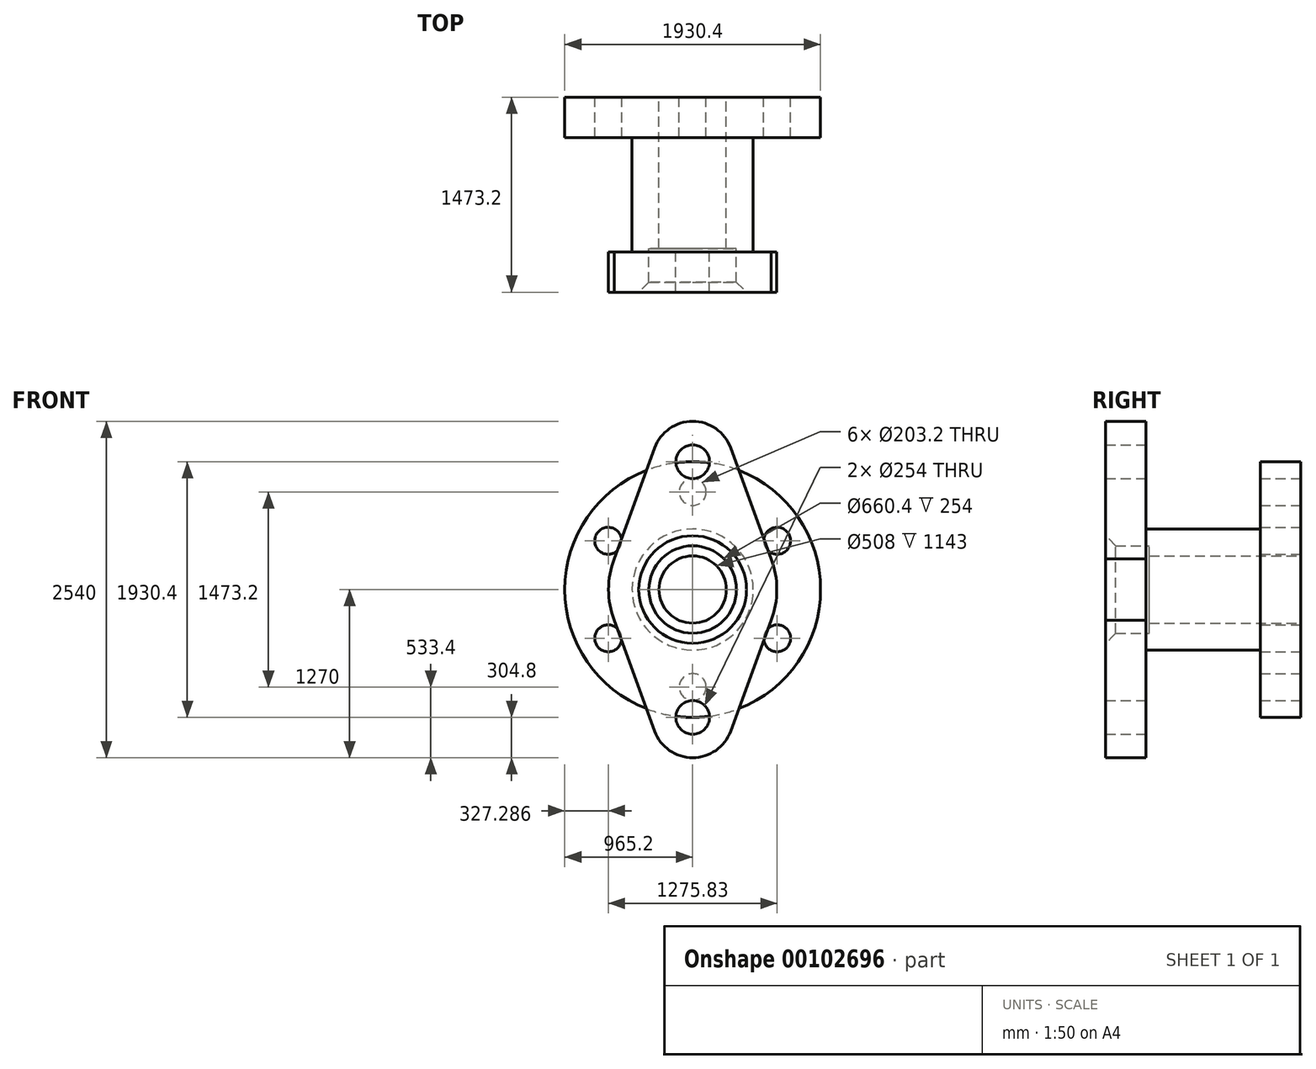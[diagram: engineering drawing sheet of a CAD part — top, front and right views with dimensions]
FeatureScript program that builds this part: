
annotation { "Feature Type Name" : "Feature", "Feature Type Description" : "" }
export const myFeature = defineFeature(function(context is Context, id is Id, definition is map)
    precondition{}
    {
        {
            var Q0;
            Q0=qCreatedBy(makeId("Front.planeOp"),FACE);
            var sketch = newSketch(context, id + "F0", { "sketchPlane" : qUnion([Q0])});
            skCircle(sketch, "E0", {"center": v(0, 0) * mm, "radius": 965.2 * mm});
            skCircle(sketch, "E1", {"center": v(0, 736.6) * mm, "radius": 101.6 * mm});
            skCircle(sketch, "E2", {"center": v(-637.91, 368.3) * mm, "radius": 101.6 * mm});
            skCircle(sketch, "E3", {"center": v(-637.91, -368.3) * mm, "radius": 101.6 * mm});
            skCircle(sketch, "E4.MirrorC", {"center": v(0, -736.6) * mm, "radius": 101.6 * mm});
            skCircle(sketch, "E5.MirrorC", {"center": v(637.91, 368.3) * mm, "radius": 101.6 * mm});
            skCircle(sketch, "E6.MirrorC", {"center": v(637.91, -368.3) * mm, "radius": 101.6 * mm});
            skCircle(sketch, "E7", {"center": v(0, 0) * mm, "radius": 254 * mm});
            skCircle(sketch, "E8", {"center": v(0, 0) * mm, "radius": 457.2 * mm});
            skCircle(sketch, "E9", {"center": v(0, 0) * mm, "radius": 330.2 * mm});
            skSolve(sketch);
        }
        {
            var Q0;
            Q0=makeQuery(id+"F0.imprint","IMPRINT",FACE,{"disambiguationData":[TD([[makeQuery(id+"F0.imprint","IMPRINT",EDGE,{"derivedFrom":sQuery(id+"F0.wireOp",EDGE,"E0")}),1.0]])]});
            extrude(context, id + "F1", {"entities" : qUnion([Q0]), "depth" : 304.8 * mm});
        }
        {
            var Q0;
            Q0=makeQuery(id+"F0.imprint","IMPRINT",FACE,{"disambiguationData":[TD([[makeQuery(id+"F0.imprint","IMPRINT",EDGE,{"derivedFrom":sQuery(id+"F0.wireOp",EDGE,"E8")}),1.0]])]});
            extrude(context, id + "F2", {"entities" : qUnion([Q0]), "operationType" : NewBodyOperationType.ADD, "depth" : 1168.4 * mm});
        }
        {
            var Q0;
            Q0=makeQuery(id+"F0.imprint","IMPRINT",FACE,{"disambiguationData":[TD([[makeQuery(id+"F0.imprint","IMPRINT",EDGE,{"derivedFrom":sQuery(id+"F0.wireOp",EDGE,"E7")}),-1.0]])]});
            extrude(context, id + "F3", {"entities" : qUnion([Q0]), "operationType" : NewBodyOperationType.ADD, "depth" : 1143 * mm});
        }
        {
            var Q0;
            Q0=makeQuery(id+"F2.opExtrude","CAP_FACE",FACE,{"disambiguationData":[OSD([sQuery(id+"F0.wireOp",EDGE,"E8"),sQuery(id+"F0.wireOp",EDGE,"E9")])],"isStart":false});
            var sketch = newSketch(context, id + "F4", { "sketchPlane" : qUnion([Q0])});
            skCircle(sketch, "E10", {"center": v(0, 0) * mm, "radius": 635 * mm});
            skLineSegment(sketch, "E11", {"start": v(0, 0) * mm, "end": v(0, 965.2) * mm});
            skCircle(sketch, "E12", {"center": v(0, 965.2) * mm, "radius": 304.8 * mm});
            skLineSegment(sketch, "E13", {"start": v(0, 0) * mm, "end": v(0, -965.2) * mm});
            skCircle(sketch, "E14", {"center": v(0, -965.2) * mm, "radius": 304.8 * mm});
            skLineSegment(sketch, "E15", {"start": v(0, 0) * mm, "end": v(330.2, 0) * mm});
            skCircle(sketch, "E16", {"center": v(0, 965.2) * mm, "radius": 127 * mm});
            skCircle(sketch, "E17", {"center": v(0, -965.2) * mm, "radius": 127 * mm});
            skLineSegment(sketch, "E18", {"start": v(591.5, 230.97) * mm, "end": v(286.43, 1069.42) * mm});
            skLineSegment(sketch, "E19", {"start": v(-591.5, 230.97) * mm, "end": v(-286.43, 1069.42) * mm});
            skLineSegment(sketch, "E20", {"start": v(-591.5, -230.97) * mm, "end": v(-286.43, -1069.42) * mm});
            skLineSegment(sketch, "E21", {"start": v(591.5, -230.97) * mm, "end": v(286.43, -1069.42) * mm});
            skSolve(sketch);
        }
        {
            var Q0;
            {var subQ1=sQuery(id+"F4.wireOp",EDGE,"E10");var subQ5=makeQuery(id+"F4.imprint","INTERSECT",VERTEX,{"derivedFrom":[subQ1,sQuery(id+"F4.wireOp",EDGE,"c6KwAkdS-stvp-whTA-LQrj-QYopWVm7Ra52")]});Q0=makeQuery(id+"F4.imprint","IMPRINT",FACE,{"disambiguationData":[TD([[makeQuery(id+"F4.imprint","IMPRINT",EDGE,{"disambiguationData":[TD([[subQ5,1.0]])],"derivedFrom":subQ1}),1.0]])]});}
            var Q1;
            {var subQ1=sQuery(id+"F4.wireOp",EDGE,"E10");var subQ5=makeQuery(id+"F4.imprint","INTERSECT",VERTEX,{"derivedFrom":[subQ1,sQuery(id+"F4.wireOp",EDGE,"JtTFtKPz-pe5b-M5Ky-iTNi-3o3Gjd6l9SQG")]});Q1=makeQuery(id+"F4.imprint","IMPRINT",FACE,{"disambiguationData":[TD([[makeQuery(id+"F4.imprint","IMPRINT",EDGE,{"disambiguationData":[TD([[subQ5,-1.0]])],"derivedFrom":subQ1}),1.0]])]});}
            var Q2;
            {var subQ0=makeQuery(id+"F2.opExtrude","CAP_EDGE",EDGE,{"disambiguationData":[OSD([sQuery(id+"F0.wireOp",EDGE,"E9")])],"isStart":false});var subQ2=sQuery(id+"F4.wireOp",EDGE,"E11");var subQ3=makeQuery(id+"F4.imprint","INTERSECT",VERTEX,{"derivedFrom":[subQ0,subQ2]});Q2=makeQuery(id+"F4.imprint","IMPRINT",FACE,{"disambiguationData":[TD([[makeQuery(id+"F4.imprint","IMPRINT",EDGE,{"disambiguationData":[TD([[subQ3,-1.0]])],"derivedFrom":subQ2}),-1.0]])]});}
            var Q3;
            {var subQ0=sQuery(id+"F4.wireOp",EDGE,"E11");var subQ1=makeQuery(id+"F2.opExtrude","CAP_EDGE",EDGE,{"disambiguationData":[OSD([sQuery(id+"F0.wireOp",EDGE,"E9")])],"isStart":false});var subQ2=makeQuery(id+"F4.imprint","INTERSECT",VERTEX,{"derivedFrom":[subQ1,subQ0]});Q3=makeQuery(id+"F4.imprint","IMPRINT",FACE,{"disambiguationData":[TD([[makeQuery(id+"F4.imprint","IMPRINT",EDGE,{"disambiguationData":[TD([[subQ2,-1.0]])],"derivedFrom":subQ0}),1.0]])]});}
            var Q4;
            {var subQ0=sQuery(id+"F4.wireOp",EDGE,"c6KwAkdS-stvp-whTA-LQrj-QYopWVm7Ra52");Q4=makeQuery(id+"F4.imprint","IMPRINT",FACE,{"disambiguationData":[TD([[makeQuery(id+"F4.imprint","IMPRINT",EDGE,{"derivedFrom":subQ0}),1.0]])]});}
            var Q5;
            Q5=makeQuery(id+"F4.imprint","IMPRINT",FACE,{"disambiguationData":[TD([[makeQuery(id+"F4.imprint","IMPRINT",EDGE,{"derivedFrom":sQuery(id+"F4.wireOp",EDGE,"E16")}),-1.0]])]});
            var Q6;
            {var subQ0=sQuery(id+"F4.wireOp",EDGE,"JtTFtKPz-pe5b-M5Ky-iTNi-3o3Gjd6l9SQG");Q6=makeQuery(id+"F4.imprint","IMPRINT",FACE,{"disambiguationData":[TD([[makeQuery(id+"F4.imprint","IMPRINT",EDGE,{"derivedFrom":subQ0}),-1.0]])]});}
            var Q7;
            {var subQ0=sQuery(id+"F4.wireOp",EDGE,"wzUlj8uY-Dt0U-XABk-br7w-0J9tpXzwqQ2q");Q7=makeQuery(id+"F4.imprint","IMPRINT",FACE,{"disambiguationData":[TD([[makeQuery(id+"F4.imprint","IMPRINT",EDGE,{"derivedFrom":subQ0}),1.0]])]});}
            var Q8;
            {var subQ0=sQuery(id+"F4.wireOp",EDGE,"q8ZmA0wt-t0vW-haXf-SDx6-wxUQsJhX23b9");Q8=makeQuery(id+"F4.imprint","IMPRINT",FACE,{"disambiguationData":[TD([[makeQuery(id+"F4.imprint","IMPRINT",EDGE,{"derivedFrom":subQ0}),-1.0]])]});}
            var Q9;
            Q9=makeQuery(id+"F4.imprint","IMPRINT",FACE,{"disambiguationData":[TD([[makeQuery(id+"F4.imprint","IMPRINT",EDGE,{"derivedFrom":sQuery(id+"F4.wireOp",EDGE,"E17")}),-1.0]])]});
            var Q10;
            {var subQ0=sQuery(id+"F4.wireOp",EDGE,"E20");Q10=makeQuery(id+"F4.imprint","IMPRINT",FACE,{"disambiguationData":[TD([[makeQuery(id+"F4.imprint","IMPRINT",EDGE,{"derivedFrom":subQ0}),1.0]])]});}
            var Q11;
            {var subQ0=sQuery(id+"F4.wireOp",EDGE,"E18");Q11=makeQuery(id+"F4.imprint","IMPRINT",FACE,{"disambiguationData":[TD([[makeQuery(id+"F4.imprint","IMPRINT",EDGE,{"derivedFrom":subQ0}),1.0]])]});}
            var Q12;
            {var subQ0=sQuery(id+"F4.wireOp",EDGE,"E19");Q12=makeQuery(id+"F4.imprint","IMPRINT",FACE,{"disambiguationData":[TD([[makeQuery(id+"F4.imprint","IMPRINT",EDGE,{"derivedFrom":subQ0}),-1.0]])]});}
            var Q13;
            {var subQ0=sQuery(id+"F4.wireOp",EDGE,"E21");Q13=makeQuery(id+"F4.imprint","IMPRINT",FACE,{"disambiguationData":[TD([[makeQuery(id+"F4.imprint","IMPRINT",EDGE,{"derivedFrom":subQ0}),-1.0]])]});}
            extrude(context, id + "F5", {"entities" : qUnion([Q0, Q1, Q2, Q3, Q4, Q5, Q6, Q7, Q8, Q9, Q10, Q11, Q12, Q13]), "operationType" : NewBodyOperationType.ADD, "depth" : 304.8 * mm});
        }
        {
            var Q0;
            Q0=makeQuery(id+"F5.opExtrude","CAP_EDGE",EDGE,{"disambiguationData":[OSD([sQuery(id+"F0.wireOp",EDGE,"E9")])],"isStart":false});
            chamfer(context, id + "F6", {"entities" : qUnion([Q0]), "chamferType" : ChamferType.OFFSET_ANGLE, "width" : 76.2 * mm, "oppositeDirection" : false, "angle" : 45 * degree, "tangentPropagation" : true});
        }
    });
